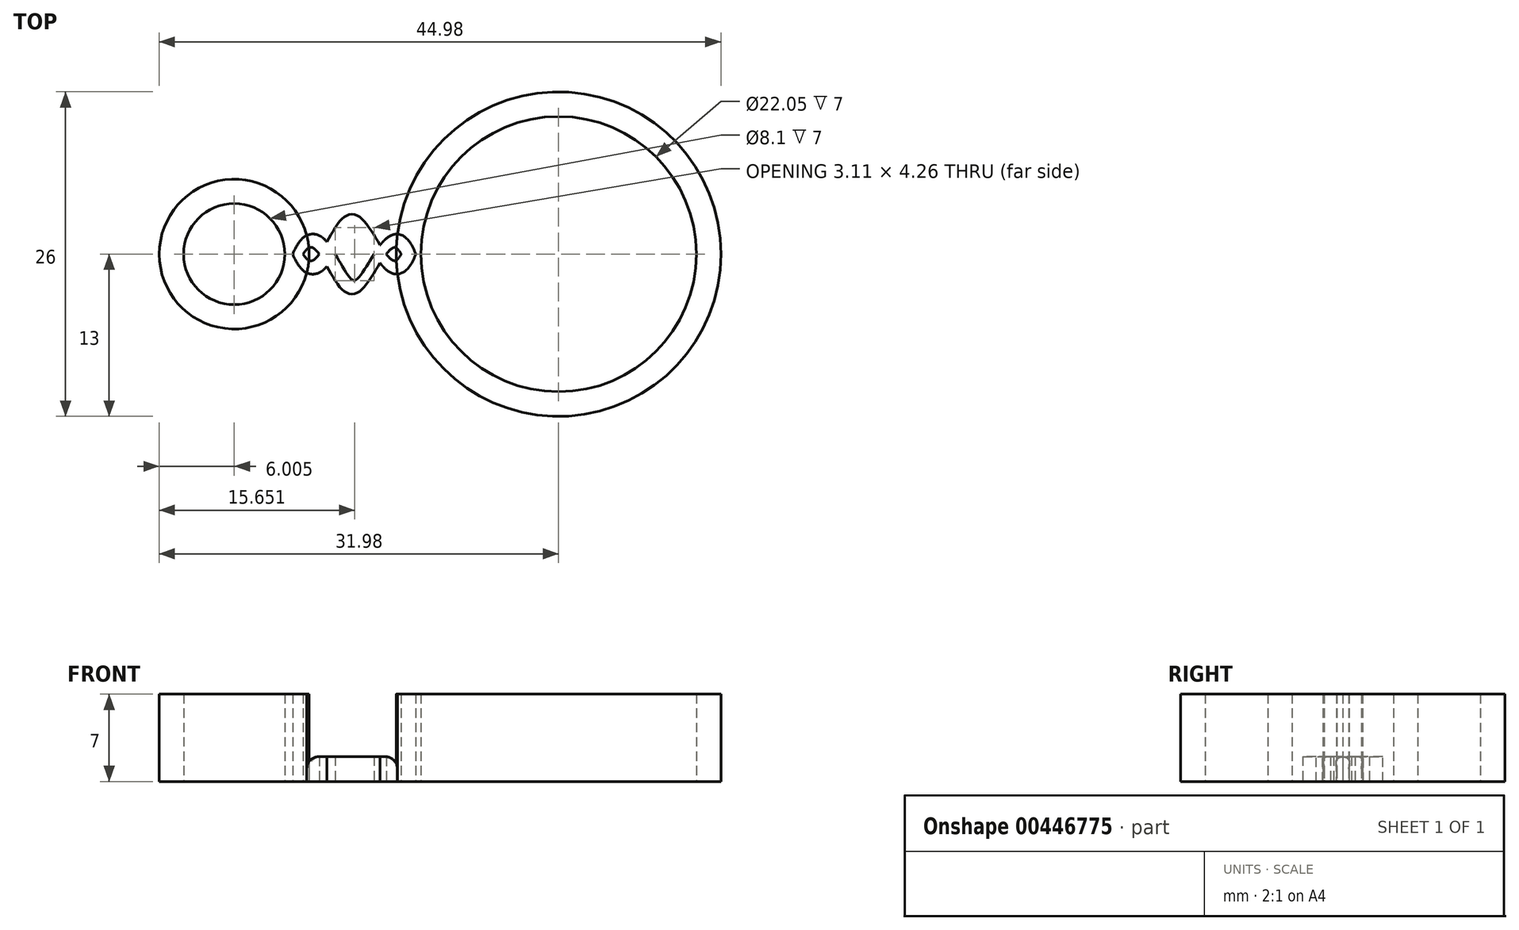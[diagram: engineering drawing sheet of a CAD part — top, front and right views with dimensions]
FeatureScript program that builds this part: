
annotation { "Feature Type Name" : "Feature", "Feature Type Description" : "" }
export const myFeature = defineFeature(function(context is Context, id is Id, definition is map)
    precondition{}
    {
        {
            var Q0;
            Q0=qCreatedBy(makeId("Top.planeOp"),FACE);
            var sketch = newSketch(context, id + "F0", { "sketchPlane" : qUnion([Q0])});
            skCircle(sketch, "E0", {"center": v(0, 0) * mm, "radius": 11.03 * mm});
            skCircle(sketch, "E1", {"center": v(0, 0) * mm, "radius": 13 * mm});
            skCircle(sketch, "E2", {"center": v(-25.97, 0) * mm, "radius": 4.05 * mm});
            skCircle(sketch, "E3", {"center": v(-25.97, 0) * mm, "radius": 6 * mm});
            skLineSegment(sketch, "E4", {"start": v(-22.2, 0) * mm, "end": v(-13, 0) * mm, "construction": true});
            skPoint(sketch, "E5", {"position": v(-17.6, 0) * mm});
            skFitSpline(sketch, "E6.0", {"points": [v(-20.78, 0.67) * mm, v(-20.67, 0.41) * mm, v(-20.45, 0) * mm, v(-20.16, -0.4) * mm, v(-19.98, -0.52) * mm, v(-19.89, -0.55) * mm, v(-19.84, -0.55) * mm, v(-19.78, -0.55) * mm, v(-19.68, -0.5) * mm, v(-19.5, -0.39) * mm, v(-19.26, -0.12) * mm, v(-19, 0.24) * mm, v(-18.74, 0.67) * mm, v(-18.48, 1.13) * mm, v(-18.2, 1.6) * mm, v(-17.94, 2.04) * mm, v(-17.66, 2.45) * mm, v(-17.42, 2.75) * mm, v(-17.2, 2.95) * mm, v(-17.01, 3.07) * mm, v(-16.8, 3.16) * mm, v(-16.55, 3.2) * mm, v(-16.3, 3.16) * mm, v(-16.1, 3.07) * mm, v(-15.9, 2.95) * mm, v(-15.68, 2.76) * mm, v(-15.42, 2.47) * mm, v(-15.13, 2.06) * mm, v(-14.84, 1.61) * mm, v(-14.55, 1.14) * mm, v(-14.27, 0.69) * mm, v(-14, 0.26) * mm, v(-13.72, -0.1) * mm, v(-13.51, -0.33) * mm, v(-13.36, -0.45) * mm, v(-13.28, -0.5) * mm, v(-13.22, -0.52) * mm, v(-13.18, -0.53) * mm, v(-13.14, -0.54) * mm, v(-13.1, -0.53) * mm, v(-13.04, -0.51) * mm, v(-12.96, -0.46) * mm, v(-12.82, -0.32) * mm, v(-12.6, 0) * mm, v(-12.42, 0.41) * mm, v(-12.32, 0.67) * mm]});
            skFitSpline(sketch, "E7.0", {"points": [v(-21.34, 0.1) * mm, v(-21.21, -0.18) * mm, v(-20.97, -0.66) * mm, v(-20.59, -1.18) * mm, v(-20.23, -1.46) * mm, v(-19.9, -1.58) * mm, v(-19.64, -1.6) * mm, v(-19.4, -1.57) * mm, v(-19.1, -1.45) * mm, v(-18.78, -1.22) * mm, v(-18.46, -0.86) * mm, v(-18.16, -0.45) * mm, v(-17.88, 0) * mm, v(-17.6, 0.48) * mm, v(-17.34, 0.94) * mm, v(-17.08, 1.37) * mm, v(-16.84, 1.73) * mm, v(-16.65, 1.95) * mm, v(-16.52, 2.06) * mm, v(-16.44, 2.1) * mm, v(-16.4, 2.13) * mm, v(-16.37, 2.13) * mm, v(-16.35, 2.13) * mm, v(-16.3, 2.1) * mm, v(-16.21, 2.06) * mm, v(-16.08, 1.94) * mm, v(-15.88, 1.72) * mm, v(-15.62, 1.36) * mm, v(-15.34, 0.93) * mm, v(-15.06, 0.47) * mm, v(-14.78, 0) * mm, v(-14.48, -0.45) * mm, v(-14.17, -0.87) * mm, v(-13.9, -1.17) * mm, v(-13.65, -1.36) * mm, v(-13.46, -1.48) * mm, v(-13.27, -1.56) * mm, v(-13.13, -1.59) * mm, v(-13.05, -1.6) * mm, v(-13, -1.6) * mm, v(-12.93, -1.6) * mm, v(-12.86, -1.6) * mm, v(-12.8, -1.59) * mm, v(-12.73, -1.57) * mm, v(-12.67, -1.56) * mm, v(-12.6, -1.53) * mm, v(-12.45, -1.46) * mm, v(-12.27, -1.34) * mm, v(-12, -1.08) * mm, v(-11.72, -0.64) * mm, v(-11.5, -0.16) * mm, v(-11.4, 0.12) * mm]});
            skPoint(sketch, "E8", {"position": v(-20.16, -1.48) * mm});
            skPoint(sketch, "E9", {"position": v(-12.9, -1.6) * mm});
            skFitSpline(sketch, "E10.MirrorCS", {"points": [v(-21.34, -0.1) * mm, v(-21.21, 0.18) * mm, v(-20.97, 0.66) * mm, v(-20.59, 1.18) * mm, v(-20.23, 1.46) * mm, v(-19.9, 1.58) * mm, v(-19.64, 1.6) * mm, v(-19.4, 1.57) * mm, v(-19.1, 1.45) * mm, v(-18.78, 1.22) * mm, v(-18.46, 0.86) * mm, v(-18.16, 0.45) * mm, v(-17.88, 0) * mm, v(-17.6, -0.48) * mm, v(-17.34, -0.94) * mm, v(-17.08, -1.37) * mm, v(-16.84, -1.73) * mm, v(-16.65, -1.95) * mm, v(-16.52, -2.06) * mm, v(-16.44, -2.1) * mm, v(-16.4, -2.13) * mm, v(-16.37, -2.13) * mm, v(-16.35, -2.13) * mm, v(-16.3, -2.1) * mm, v(-16.21, -2.06) * mm, v(-16.08, -1.94) * mm, v(-15.88, -1.72) * mm, v(-15.62, -1.36) * mm, v(-15.34, -0.93) * mm, v(-15.06, -0.47) * mm, v(-14.78, 0) * mm, v(-14.48, 0.45) * mm, v(-14.17, 0.87) * mm, v(-13.9, 1.17) * mm, v(-13.65, 1.36) * mm, v(-13.46, 1.48) * mm, v(-13.27, 1.56) * mm, v(-13.13, 1.59) * mm, v(-13.05, 1.6) * mm, v(-13, 1.6) * mm, v(-12.93, 1.6) * mm, v(-12.86, 1.6) * mm, v(-12.8, 1.59) * mm, v(-12.73, 1.57) * mm, v(-12.67, 1.56) * mm, v(-12.6, 1.53) * mm, v(-12.45, 1.46) * mm, v(-12.27, 1.34) * mm, v(-12, 1.08) * mm, v(-11.72, 0.64) * mm, v(-11.5, 0.16) * mm, v(-11.4, -0.12) * mm]});
            skFitSpline(sketch, "E11.MirrorCS", {"points": [v(-20.78, -0.67) * mm, v(-20.67, -0.41) * mm, v(-20.45, 0) * mm, v(-20.16, 0.4) * mm, v(-19.98, 0.52) * mm, v(-19.89, 0.55) * mm, v(-19.84, 0.55) * mm, v(-19.78, 0.55) * mm, v(-19.68, 0.5) * mm, v(-19.5, 0.39) * mm, v(-19.26, 0.12) * mm, v(-19, -0.24) * mm, v(-18.74, -0.67) * mm, v(-18.48, -1.13) * mm, v(-18.2, -1.6) * mm, v(-17.94, -2.04) * mm, v(-17.66, -2.45) * mm, v(-17.42, -2.75) * mm, v(-17.2, -2.95) * mm, v(-17.01, -3.07) * mm, v(-16.8, -3.16) * mm, v(-16.55, -3.2) * mm, v(-16.3, -3.16) * mm, v(-16.1, -3.07) * mm, v(-15.9, -2.95) * mm, v(-15.68, -2.76) * mm, v(-15.42, -2.47) * mm, v(-15.13, -2.06) * mm, v(-14.84, -1.61) * mm, v(-14.55, -1.14) * mm, v(-14.27, -0.69) * mm, v(-14, -0.26) * mm, v(-13.72, 0.1) * mm, v(-13.51, 0.33) * mm, v(-13.36, 0.45) * mm, v(-13.28, 0.5) * mm, v(-13.22, 0.52) * mm, v(-13.18, 0.53) * mm, v(-13.14, 0.54) * mm, v(-13.1, 0.53) * mm, v(-13.04, 0.51) * mm, v(-12.96, 0.46) * mm, v(-12.82, 0.32) * mm, v(-12.6, 0) * mm, v(-12.42, -0.41) * mm, v(-12.32, -0.67) * mm]});
            skSolve(sketch);
        }
        {
            var Q0;
            {var subQ0=sQuery(id+"F0.wireOp",EDGE,"E11.MirrorCS");var subQ1=sQuery(id+"F0.wireOp",EDGE,"E6.0");var subQ2=makeQuery(id+"F0.imprint","INTERSECT",VERTEX,{"disambiguationData":[OD(2.0)],"derivedFrom":[subQ1,subQ0]});Q0=makeQuery(id+"F0.imprint","IMPRINT",FACE,{"disambiguationData":[TD([[makeQuery(id+"F0.imprint","IMPRINT",EDGE,{"disambiguationData":[TD([[subQ2,-1.0]])],"derivedFrom":subQ1}),-1.0]])]});}
            var Q1;
            {var subQ0=sQuery(id+"F0.wireOp",EDGE,"E10.MirrorCS");var subQ1=sQuery(id+"F0.wireOp",EDGE,"E6.0");var subQ2=makeQuery(id+"F0.imprint","INTERSECT",VERTEX,{"disambiguationData":[OD(0.0)],"derivedFrom":[subQ1,subQ0]});Q1=makeQuery(id+"F0.imprint","IMPRINT",FACE,{"disambiguationData":[TD([[makeQuery(id+"F0.imprint","IMPRINT",EDGE,{"disambiguationData":[TD([[subQ2,-1.0]])],"derivedFrom":subQ1}),-1.0]])]});}
            var Q2;
            {var subQ0=sQuery(id+"F0.wireOp",EDGE,"E10.MirrorCS");var subQ1=sQuery(id+"F0.wireOp",EDGE,"E6.0");var subQ2=makeQuery(id+"F0.imprint","INTERSECT",VERTEX,{"disambiguationData":[OD(1.0)],"derivedFrom":[subQ1,subQ0]});Q2=makeQuery(id+"F0.imprint","IMPRINT",FACE,{"disambiguationData":[TD([[makeQuery(id+"F0.imprint","IMPRINT",EDGE,{"disambiguationData":[TD([[subQ2,-1.0]])],"derivedFrom":subQ1}),-1.0]])]});}
            var Q3;
            {var subQ0=sQuery(id+"F0.wireOp",EDGE,"E10.MirrorCS");var subQ1=sQuery(id+"F0.wireOp",EDGE,"E6.0");var subQ2=makeQuery(id+"F0.imprint","INTERSECT",VERTEX,{"disambiguationData":[OD(0.0)],"derivedFrom":[subQ1,subQ0]});Q3=makeQuery(id+"F0.imprint","IMPRINT",FACE,{"disambiguationData":[TD([[makeQuery(id+"F0.imprint","IMPRINT",EDGE,{"disambiguationData":[TD([[subQ2,-1.0]])],"derivedFrom":subQ1}),-1.0]])]});}
            var Q4;
            {var subQ0=sQuery(id+"F0.wireOp",EDGE,"E7.0");var subQ1=sQuery(id+"F0.wireOp",EDGE,"E1");var subQ2=makeQuery(id+"F0.imprint","INTERSECT",VERTEX,{"derivedFrom":[subQ1,subQ0]});Q4=makeQuery(id+"F0.imprint","IMPRINT",FACE,{"disambiguationData":[TD([[makeQuery(id+"F0.imprint","IMPRINT",EDGE,{"disambiguationData":[TD([[subQ2,1.0]])],"derivedFrom":subQ1}),-1.0]])]});}
            var Q5;
            {var subQ0=sQuery(id+"F0.wireOp",EDGE,"E10.MirrorCS");var subQ1=sQuery(id+"F0.wireOp",EDGE,"E6.0");var subQ2=makeQuery(id+"F0.imprint","INTERSECT",VERTEX,{"disambiguationData":[OD(1.0)],"derivedFrom":[subQ1,subQ0]});Q5=makeQuery(id+"F0.imprint","IMPRINT",FACE,{"disambiguationData":[TD([[makeQuery(id+"F0.imprint","IMPRINT",EDGE,{"disambiguationData":[TD([[subQ2,-1.0]])],"derivedFrom":subQ1}),-1.0]])]});}
            var Q6;
            {var subQ0=sQuery(id+"F0.wireOp",EDGE,"E11.MirrorCS");var subQ1=sQuery(id+"F0.wireOp",EDGE,"E7.0");var subQ2=makeQuery(id+"F0.imprint","INTERSECT",VERTEX,{"disambiguationData":[OD(0.0)],"derivedFrom":[subQ1,subQ0]});Q6=makeQuery(id+"F0.imprint","IMPRINT",FACE,{"disambiguationData":[TD([[makeQuery(id+"F0.imprint","IMPRINT",EDGE,{"disambiguationData":[TD([[subQ2,-1.0]])],"derivedFrom":subQ1}),-1.0]])]});}
            var Q7;
            {var subQ0=sQuery(id+"F0.wireOp",EDGE,"E11.MirrorCS");var subQ1=sQuery(id+"F0.wireOp",EDGE,"E6.0");var subQ2=makeQuery(id+"F0.imprint","INTERSECT",VERTEX,{"disambiguationData":[OD(2.0)],"derivedFrom":[subQ1,subQ0]});Q7=makeQuery(id+"F0.imprint","IMPRINT",FACE,{"disambiguationData":[TD([[makeQuery(id+"F0.imprint","IMPRINT",EDGE,{"disambiguationData":[TD([[subQ2,-1.0]])],"derivedFrom":subQ1}),-1.0]])]});}
            var Q8;
            {var subQ0=sQuery(id+"F0.wireOp",EDGE,"E7.0");var subQ1=sQuery(id+"F0.wireOp",EDGE,"E3");var subQ2=makeQuery(id+"F0.imprint","INTERSECT",VERTEX,{"derivedFrom":[subQ1,subQ0]});Q8=makeQuery(id+"F0.imprint","IMPRINT",FACE,{"disambiguationData":[TD([[makeQuery(id+"F0.imprint","IMPRINT",EDGE,{"disambiguationData":[TD([[subQ2,-1.0]])],"derivedFrom":subQ1}),-1.0]])]});}
            var Q9;
            {var subQ0=sQuery(id+"F0.wireOp",EDGE,"E10.MirrorCS");var subQ1=sQuery(id+"F0.wireOp",EDGE,"E3");var subQ2=makeQuery(id+"F0.imprint","INTERSECT",VERTEX,{"derivedFrom":[subQ1,subQ0]});Q9=makeQuery(id+"F0.imprint","IMPRINT",FACE,{"disambiguationData":[TD([[makeQuery(id+"F0.imprint","IMPRINT",EDGE,{"disambiguationData":[TD([[subQ2,1.0]])],"derivedFrom":subQ1}),-1.0]])]});}
            var Q10;
            {var subQ0=sQuery(id+"F0.wireOp",EDGE,"E10.MirrorCS");var subQ1=sQuery(id+"F0.wireOp",EDGE,"E1");var subQ2=makeQuery(id+"F0.imprint","INTERSECT",VERTEX,{"derivedFrom":[subQ1,subQ0]});Q10=makeQuery(id+"F0.imprint","IMPRINT",FACE,{"disambiguationData":[TD([[makeQuery(id+"F0.imprint","IMPRINT",EDGE,{"disambiguationData":[TD([[subQ2,-1.0]])],"derivedFrom":subQ1}),-1.0]])]});}
            extrude(context, id + "F1", {"entities" : qUnion([Q0, Q1, Q2, Q3, Q4, Q5, Q6, Q7, Q8, Q9, Q10]), "depth" : 2 * mm});
        }
        {
            var Q0;
            Q0=makeQuery(id+"F0.imprint","IMPRINT",FACE,{"disambiguationData":[TD([[makeQuery(id+"F0.imprint","IMPRINT",EDGE,{"derivedFrom":sQuery(id+"F0.wireOp",EDGE,"E2")}),-1.0]])]});
            var Q1;
            Q1=makeQuery(id+"F0.imprint","IMPRINT",FACE,{"disambiguationData":[TD([[makeQuery(id+"F0.imprint","IMPRINT",EDGE,{"derivedFrom":sQuery(id+"F0.wireOp",EDGE,"E0")}),-1.0]])]});
            var Q2;
            {var subQ0=sQuery(id+"F0.wireOp",EDGE,"E11.MirrorCS");var subQ1=sQuery(id+"F0.wireOp",EDGE,"E3");var subQ2=makeQuery(id+"F0.imprint","INTERSECT",VERTEX,{"derivedFrom":[subQ1,subQ0]});Q2=makeQuery(id+"F0.imprint","IMPRINT",FACE,{"disambiguationData":[TD([[makeQuery(id+"F0.imprint","IMPRINT",EDGE,{"disambiguationData":[TD([[subQ2,1.0]])],"derivedFrom":subQ1}),1.0]])]});}
            var Q3;
            {var subQ0=sQuery(id+"F0.wireOp",EDGE,"E11.MirrorCS");var subQ1=sQuery(id+"F0.wireOp",EDGE,"E1");var subQ2=makeQuery(id+"F0.imprint","INTERSECT",VERTEX,{"derivedFrom":[subQ1,subQ0]});Q3=makeQuery(id+"F0.imprint","IMPRINT",FACE,{"disambiguationData":[TD([[makeQuery(id+"F0.imprint","IMPRINT",EDGE,{"disambiguationData":[TD([[subQ2,-1.0]])],"derivedFrom":subQ1}),1.0]])]});}
            extrude(context, id + "F2", {"entities" : qUnion([Q0, Q1, Q2, Q3]), "operationType" : NewBodyOperationType.ADD, "depth" : 7 * mm});
        }
        {
            var Q0;
            {var subQ0=sQuery(id+"F0.wireOp",EDGE,"E3");Q0=makeQuery(id+"F1.opExtrude","CAP_EDGE",EDGE,{"disambiguationData":[OSD([subQ0]),TDD([makeQuery(id+"F0.imprint","IMPRINT",EDGE,{"disambiguationData":[TD([[makeQuery(id+"F0.imprint","INTERSECT",VERTEX,{"derivedFrom":[subQ0,sQuery(id+"F0.wireOp",EDGE,"E7.0")]}),-1.0]])],"derivedFrom":subQ0})])],"isStart":false});}
            var Q1;
            {var subQ0=sQuery(id+"F0.wireOp",EDGE,"E1");Q1=makeQuery(id+"F1.opExtrude","CAP_EDGE",EDGE,{"disambiguationData":[OSD([subQ0]),TDD([makeQuery(id+"F0.imprint","IMPRINT",EDGE,{"disambiguationData":[TD([[makeQuery(id+"F0.imprint","INTERSECT",VERTEX,{"derivedFrom":[subQ0,sQuery(id+"F0.wireOp",EDGE,"E7.0")]}),1.0]])],"derivedFrom":subQ0})])],"isStart":false});}
            fillet(context, id + "F3", {"entities" : qUnion([Q0, Q1]), "radius" : 1 * mm, "tangentPropagation" : true, "allowEdgeOverflow" : false});
        }
    });
